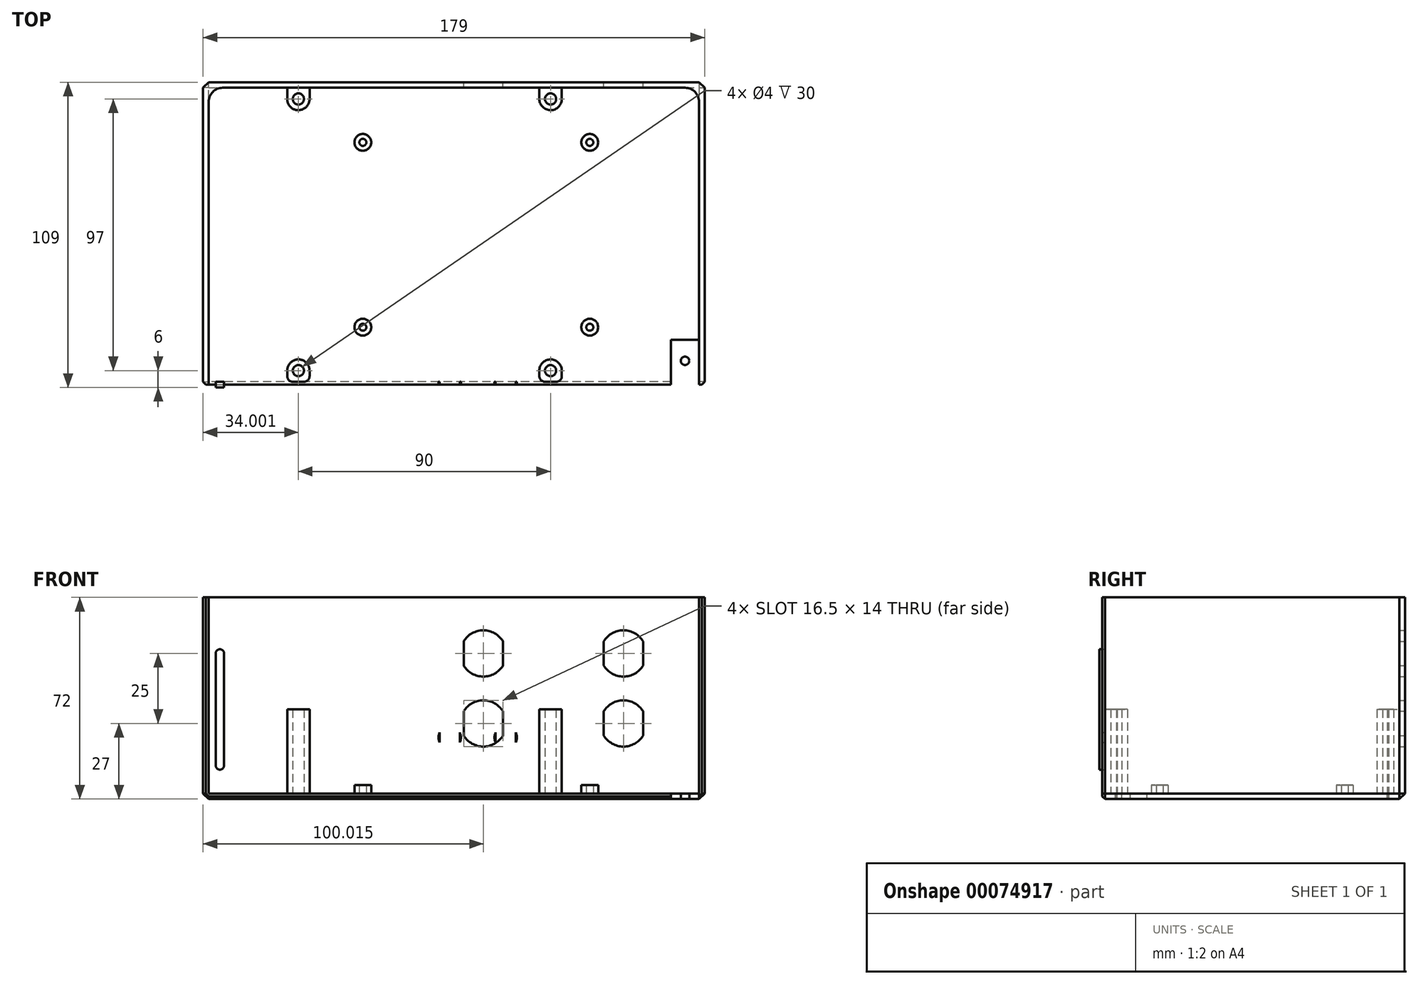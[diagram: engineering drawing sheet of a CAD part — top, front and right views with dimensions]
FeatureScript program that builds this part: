
annotation { "Feature Type Name" : "Feature", "Feature Type Description" : "" }
export const myFeature = defineFeature(function(context is Context, id is Id, definition is map)
    precondition{}
    {
        {
            var Q0;
            Q0=qCreatedBy(makeId("Top.planeOp"),FACE);
            var sketch = newSketch(context, id + "F0", { "sketchPlane" : qUnion([Q0])});
            skLineSegment(sketch, "E0.bottom", {"start": v(-80.27, 52.5) * mm, "end": v(94.73, 52.5) * mm});
            skLineSegment(sketch, "E0.top", {"start": v(-80.27, -52.5) * mm, "end": v(94.73, -52.5) * mm});
            skLineSegment(sketch, "E0.left", {"start": v(-80.27, 52.5) * mm, "end": v(-80.27, -52.5) * mm});
            skLineSegment(sketch, "E0.right", {"start": v(94.73, 52.5) * mm, "end": v(94.73, -52.5) * mm});
            skCircle(sketch, "E1", {"center": v(-25.27, 33) * mm, "radius": 1.25 * mm});
            skCircle(sketch, "E2.0.1.0", {"center": v(-25.27, -33) * mm, "radius": 1.25 * mm});
            skCircle(sketch, "E2.1.0.0", {"center": v(55.73, 33) * mm, "radius": 1.25 * mm});
            skCircle(sketch, "E2.1.1.0", {"center": v(55.73, -33) * mm, "radius": 1.25 * mm});
            skLineSegment(sketch, "E2.direction1", {"start": v(-25.27, 33) * mm, "end": v(55.73, 33) * mm, "construction": true});
            skLineSegment(sketch, "E2.direction2", {"start": v(-25.27, 33) * mm, "end": v(-25.27, -33) * mm, "construction": true});
            skLineSegment(sketch, "E3.bottom", {"start": v(-82.27, 54.5) * mm, "end": v(96.73, 54.5) * mm});
            skLineSegment(sketch, "E3.top", {"start": v(-82.27, -54.5) * mm, "end": v(96.73, -54.5) * mm});
            skLineSegment(sketch, "E3.left", {"start": v(-82.27, 54.5) * mm, "end": v(-82.27, -54.5) * mm});
            skLineSegment(sketch, "E3.right", {"start": v(96.73, 54.5) * mm, "end": v(96.73, -54.5) * mm});
            skCircle(sketch, "E4", {"center": v(-25.27, 33) * mm, "radius": 3 * mm});
            skCircle(sketch, "E5.0.1.0", {"center": v(-25.27, -33) * mm, "radius": 3 * mm});
            skCircle(sketch, "E5.1.0.0", {"center": v(55.73, 33) * mm, "radius": 3 * mm});
            skCircle(sketch, "E5.1.1.0", {"center": v(55.73, -33) * mm, "radius": 3 * mm});
            skLineSegment(sketch, "E6.bottom", {"start": v(-48.27, 42.5) * mm, "end": v(75.73, 42.5) * mm});
            skLineSegment(sketch, "E6.top", {"start": v(-48.27, -42.5) * mm, "end": v(75.73, -42.5) * mm});
            skLineSegment(sketch, "E6.left", {"start": v(-48.27, 42.5) * mm, "end": v(-48.27, -42.5) * mm});
            skLineSegment(sketch, "E6.right", {"start": v(75.73, 42.5) * mm, "end": v(75.73, -42.5) * mm});
            skCircle(sketch, "E7", {"center": v(-48.27, -48.5) * mm, "radius": 2 * mm});
            skCircle(sketch, "E8", {"center": v(-48.27, -48.5) * mm, "radius": 4 * mm});
            skCircle(sketch, "E9.0.1.0", {"center": v(-48.27, 48.5) * mm, "radius": 4 * mm});
            skCircle(sketch, "E9.0.1.1", {"center": v(-48.27, 48.5) * mm, "radius": 2 * mm});
            skCircle(sketch, "E9.1.0.0", {"center": v(41.73, -48.5) * mm, "radius": 4 * mm});
            skCircle(sketch, "E9.1.0.1", {"center": v(41.73, -48.5) * mm, "radius": 2 * mm});
            skCircle(sketch, "E9.1.1.0", {"center": v(41.73, 48.5) * mm, "radius": 4 * mm});
            skCircle(sketch, "E9.1.1.1", {"center": v(41.73, 48.5) * mm, "radius": 2 * mm});
            skLineSegment(sketch, "E9.direction1", {"start": v(-48.27, -48.5) * mm, "end": v(41.73, -48.5) * mm, "construction": true});
            skLineSegment(sketch, "E9.direction2", {"start": v(-48.27, -48.5) * mm, "end": v(-48.27, 48.5) * mm, "construction": true});
            skLineSegment(sketch, "E10", {"start": v(-52.27, -48.55) * mm, "end": v(-52.22, -52.5) * mm});
            skLineSegment(sketch, "E11", {"start": v(-44.27, -48.5) * mm, "end": v(-44.27, -52.5) * mm});
            skLineSegment(sketch, "E12", {"start": v(-52.26, 48.76) * mm, "end": v(-52.26, 52.5) * mm});
            skLineSegment(sketch, "E13", {"start": v(-44.27, 48.54) * mm, "end": v(-44.27, 52.5) * mm});
            skLineSegment(sketch, "E14", {"start": v(37.74, 48.16) * mm, "end": v(37.74, 52.5) * mm});
            skLineSegment(sketch, "E15", {"start": v(45.73, 48.44) * mm, "end": v(45.73, 52.5) * mm});
            skLineSegment(sketch, "E16.MirrorCS", {"start": v(37.74, -48.16) * mm, "end": v(37.74, -52.5) * mm});
            skLineSegment(sketch, "E17.MirrorCS", {"start": v(45.73, -48.44) * mm, "end": v(45.73, -52.5) * mm});
            skLineSegment(sketch, "E18.bottom", {"start": v(94.73, 27.5) * mm, "end": v(84.73, 27.5) * mm});
            skLineSegment(sketch, "E18.top", {"start": v(94.73, 12.5) * mm, "end": v(84.73, 12.5) * mm});
            skLineSegment(sketch, "E18.left", {"start": v(94.73, 27.5) * mm, "end": v(94.73, 12.5) * mm});
            skLineSegment(sketch, "E18.right", {"start": v(84.73, 27.5) * mm, "end": v(84.73, 12.5) * mm});
            skCircle(sketch, "E19", {"center": v(89.73, 20) * mm, "radius": 1.5 * mm});
            skPoint(sketch, "E19.centerSnap0", {"position": v(89.73, 12.5) * mm});
            skPoint(sketch, "E19.centerSnap1", {"position": v(94.73, 20) * mm});
            skLineSegment(sketch, "E20.bottom", {"start": v(94.73, -52.5) * mm, "end": v(84.73, -52.5) * mm});
            skLineSegment(sketch, "E20.top", {"start": v(94.73, -37.5) * mm, "end": v(84.73, -37.5) * mm});
            skLineSegment(sketch, "E20.left", {"start": v(94.73, -52.5) * mm, "end": v(94.73, -37.5) * mm});
            skLineSegment(sketch, "E20.right", {"start": v(84.73, -52.5) * mm, "end": v(84.73, -37.5) * mm});
            skCircle(sketch, "E21", {"center": v(89.73, -45) * mm, "radius": 1.5 * mm});
            skPoint(sketch, "E21.centerSnap0", {"position": v(94.73, -45) * mm});
            skPoint(sketch, "E21.centerSnap1", {"position": v(89.73, -52.5) * mm});
            skSolve(sketch);
        }
        {
            var Q0;
            Q0 = qSketchRegion(id + "F0", true);
            var Q1;
            Q1=makeQuery(id+"F0.imprint","IMPRINT",FACE,{"disambiguationData":[TD([[makeQuery(id+"F0.imprint","IMPRINT",EDGE,{"derivedFrom":sQuery(id+"F0.wireOp",EDGE,"E0.bottom")}),-1.0]])]});
            var Q2;
            Q2=makeQuery(id+"F0.imprint","IMPRINT",FACE,{"disambiguationData":[TD([[makeQuery(id+"F0.imprint","IMPRINT",EDGE,{"derivedFrom":sQuery(id+"F0.wireOp",EDGE,"E2.1.1.0")}),-1.0]])]});
            var Q3;
            Q3=makeQuery(id+"F0.imprint","IMPRINT",FACE,{"disambiguationData":[TD([[makeQuery(id+"F0.imprint","IMPRINT",EDGE,{"derivedFrom":sQuery(id+"F0.wireOp",EDGE,"E2.1.1.0")}),1.0]])]});
            var Q4;
            Q4=makeQuery(id+"F0.imprint","IMPRINT",FACE,{"disambiguationData":[TD([[makeQuery(id+"F0.imprint","IMPRINT",EDGE,{"derivedFrom":sQuery(id+"F0.wireOp",EDGE,"E2.0.1.0")}),-1.0]])]});
            var Q5;
            Q5=makeQuery(id+"F0.imprint","IMPRINT",FACE,{"disambiguationData":[TD([[makeQuery(id+"F0.imprint","IMPRINT",EDGE,{"derivedFrom":sQuery(id+"F0.wireOp",EDGE,"E2.0.1.0")}),1.0]])]});
            var Q6;
            Q6=makeQuery(id+"F0.imprint","IMPRINT",FACE,{"disambiguationData":[TD([[makeQuery(id+"F0.imprint","IMPRINT",EDGE,{"derivedFrom":sQuery(id+"F0.wireOp",EDGE,"E1")}),-1.0]])]});
            var Q7;
            Q7=makeQuery(id+"F0.imprint","IMPRINT",FACE,{"disambiguationData":[TD([[makeQuery(id+"F0.imprint","IMPRINT",EDGE,{"derivedFrom":sQuery(id+"F0.wireOp",EDGE,"E1")}),1.0]])]});
            var Q8;
            Q8=makeQuery(id+"F0.imprint","IMPRINT",FACE,{"disambiguationData":[TD([[makeQuery(id+"F0.imprint","IMPRINT",EDGE,{"derivedFrom":sQuery(id+"F0.wireOp",EDGE,"E2.1.0.0")}),-1.0]])]});
            var Q9;
            Q9=makeQuery(id+"F0.imprint","IMPRINT",FACE,{"disambiguationData":[TD([[makeQuery(id+"F0.imprint","IMPRINT",EDGE,{"derivedFrom":sQuery(id+"F0.wireOp",EDGE,"E2.1.0.0")}),1.0]])]});
            var Q10;
            Q10=makeQuery(id+"F0.imprint","IMPRINT",FACE,{"disambiguationData":[TD([[makeQuery(id+"F0.imprint","IMPRINT",EDGE,{"derivedFrom":sQuery(id+"F0.wireOp",EDGE,"E4")}),-1.0]])]});
            var Q11;
            Q11=makeQuery(id+"F0.imprint","IMPRINT",FACE,{"disambiguationData":[TD([[makeQuery(id+"F0.imprint","IMPRINT",EDGE,{"derivedFrom":sQuery(id+"F0.wireOp",EDGE,"E9.1.0.1")}),-1.0]])]});
            var Q12;
            Q12=makeQuery(id+"F0.imprint","IMPRINT",FACE,{"disambiguationData":[TD([[makeQuery(id+"F0.imprint","IMPRINT",EDGE,{"derivedFrom":sQuery(id+"F0.wireOp",EDGE,"E9.1.0.1")}),1.0]])]});
            var Q13;
            {var subQ0=sQuery(id+"F0.wireOp",EDGE,"E16.MirrorCS");var subQ1=sQuery(id+"F0.wireOp",EDGE,"E0.top");var subQ2=makeQuery(id+"F0.imprint","INTERSECT",VERTEX,{"derivedFrom":[subQ1,subQ0]});Q13=makeQuery(id+"F0.imprint","IMPRINT",FACE,{"disambiguationData":[TD([[makeQuery(id+"F0.imprint","IMPRINT",EDGE,{"disambiguationData":[TD([[subQ2,-1.0]])],"derivedFrom":subQ1}),1.0]])]});}
            var Q14;
            Q14=makeQuery(id+"F0.imprint","IMPRINT",FACE,{"disambiguationData":[TD([[makeQuery(id+"F0.imprint","IMPRINT",EDGE,{"derivedFrom":sQuery(id+"F0.wireOp",EDGE,"E7")}),-1.0]])]});
            var Q15;
            Q15=makeQuery(id+"F0.imprint","IMPRINT",FACE,{"disambiguationData":[TD([[makeQuery(id+"F0.imprint","IMPRINT",EDGE,{"derivedFrom":sQuery(id+"F0.wireOp",EDGE,"E7")}),1.0]])]});
            var Q16;
            {var subQ0=sQuery(id+"F0.wireOp",EDGE,"E10");Q16=makeQuery(id+"F0.imprint","IMPRINT",FACE,{"disambiguationData":[TD([[makeQuery(id+"F0.imprint","IMPRINT",EDGE,{"derivedFrom":subQ0}),1.0]])]});}
            var Q17;
            {var subQ0=sQuery(id+"F0.wireOp",EDGE,"E11");Q17=makeQuery(id+"F0.imprint","IMPRINT",FACE,{"disambiguationData":[TD([[makeQuery(id+"F0.imprint","IMPRINT",EDGE,{"derivedFrom":subQ0}),-1.0]])]});}
            var Q18;
            Q18=makeQuery(id+"F0.imprint","IMPRINT",FACE,{"disambiguationData":[TD([[makeQuery(id+"F0.imprint","IMPRINT",EDGE,{"derivedFrom":sQuery(id+"F0.wireOp",EDGE,"E9.0.1.1")}),-1.0]])]});
            var Q19;
            Q19=makeQuery(id+"F0.imprint","IMPRINT",FACE,{"disambiguationData":[TD([[makeQuery(id+"F0.imprint","IMPRINT",EDGE,{"derivedFrom":sQuery(id+"F0.wireOp",EDGE,"E9.0.1.1")}),1.0]])]});
            var Q20;
            {var subQ0=sQuery(id+"F0.wireOp",EDGE,"E13");Q20=makeQuery(id+"F0.imprint","IMPRINT",FACE,{"disambiguationData":[TD([[makeQuery(id+"F0.imprint","IMPRINT",EDGE,{"derivedFrom":subQ0}),1.0]])]});}
            var Q21;
            {var subQ0=sQuery(id+"F0.wireOp",EDGE,"E12");Q21=makeQuery(id+"F0.imprint","IMPRINT",FACE,{"disambiguationData":[TD([[makeQuery(id+"F0.imprint","IMPRINT",EDGE,{"derivedFrom":subQ0}),-1.0]])]});}
            var Q22;
            {var subQ0=sQuery(id+"F0.wireOp",EDGE,"E17.MirrorCS");var subQ1=sQuery(id+"F0.wireOp",EDGE,"E0.top");var subQ2=makeQuery(id+"F0.imprint","INTERSECT",VERTEX,{"derivedFrom":[subQ1,subQ0]});Q22=makeQuery(id+"F0.imprint","IMPRINT",FACE,{"disambiguationData":[TD([[makeQuery(id+"F0.imprint","IMPRINT",EDGE,{"disambiguationData":[TD([[subQ2,1.0]])],"derivedFrom":subQ1}),1.0]])]});}
            var Q23;
            {var subQ0=sQuery(id+"F0.wireOp",EDGE,"E14");var subQ1=sQuery(id+"F0.wireOp",EDGE,"E0.bottom");var subQ2=makeQuery(id+"F0.imprint","INTERSECT",VERTEX,{"derivedFrom":[subQ1,subQ0]});Q23=makeQuery(id+"F0.imprint","IMPRINT",FACE,{"disambiguationData":[TD([[makeQuery(id+"F0.imprint","IMPRINT",EDGE,{"disambiguationData":[TD([[subQ2,-1.0]])],"derivedFrom":subQ1}),-1.0]])]});}
            var Q24;
            {var subQ0=sQuery(id+"F0.wireOp",EDGE,"E15");var subQ1=sQuery(id+"F0.wireOp",EDGE,"E0.bottom");var subQ2=makeQuery(id+"F0.imprint","INTERSECT",VERTEX,{"derivedFrom":[subQ1,subQ0]});Q24=makeQuery(id+"F0.imprint","IMPRINT",FACE,{"disambiguationData":[TD([[makeQuery(id+"F0.imprint","IMPRINT",EDGE,{"disambiguationData":[TD([[subQ2,1.0]])],"derivedFrom":subQ1}),-1.0]])]});}
            var Q25;
            Q25=makeQuery(id+"F0.imprint","IMPRINT",FACE,{"disambiguationData":[TD([[makeQuery(id+"F0.imprint","IMPRINT",EDGE,{"derivedFrom":sQuery(id+"F0.wireOp",EDGE,"E9.1.1.1")}),-1.0]])]});
            var Q26;
            Q26=makeQuery(id+"F0.imprint","IMPRINT",FACE,{"disambiguationData":[TD([[makeQuery(id+"F0.imprint","IMPRINT",EDGE,{"derivedFrom":sQuery(id+"F0.wireOp",EDGE,"E9.1.1.1")}),1.0]])]});
            var Q27;
            Q27=makeQuery(id+"F0.imprint","IMPRINT",FACE,{"disambiguationData":[TD([[makeQuery(id+"F0.imprint","IMPRINT",EDGE,{"derivedFrom":sQuery(id+"F0.wireOp",EDGE,"E18.bottom")}),1.0]])]});
            var Q28;
            Q28=makeQuery(id+"F0.imprint","IMPRINT",FACE,{"disambiguationData":[TD([[makeQuery(id+"F0.imprint","IMPRINT",EDGE,{"derivedFrom":sQuery(id+"F0.wireOp",EDGE,"E20.bottom")}),-1.0]])]});
            var Q29;
            Q29=makeQuery(id+"F0.imprint","IMPRINT",FACE,{"disambiguationData":[TD([[makeQuery(id+"F0.imprint","IMPRINT",EDGE,{"derivedFrom":sQuery(id+"F0.wireOp",EDGE,"E19")}),1.0]])]});
            var Q30;
            Q30=makeQuery(id+"F0.imprint","IMPRINT",FACE,{"disambiguationData":[TD([[makeQuery(id+"F0.imprint","IMPRINT",EDGE,{"derivedFrom":sQuery(id+"F0.wireOp",EDGE,"E21")}),1.0]])]});
            extrude(context, id + "F1", {"entities" : qUnion([Q0, Q1, Q2, Q3, Q4, Q5, Q6, Q7, Q8, Q9, Q10, Q11, Q12, Q13, Q14, Q15, Q16, Q17, Q18, Q19, Q20, Q21, Q22, Q23, Q24, Q25, Q26, Q27, Q28, Q29, Q30]), "oppositeDirection" : true, "depth" : 2 * mm});
        }
        {
            var Q0;
            Q0=makeQuery(id+"F0.imprint","IMPRINT",FACE,{"disambiguationData":[TD([[makeQuery(id+"F0.imprint","IMPRINT",EDGE,{"derivedFrom":sQuery(id+"F0.wireOp",EDGE,"E1")}),-1.0]])]});
            var Q1;
            Q1=makeQuery(id+"F0.imprint","IMPRINT",FACE,{"disambiguationData":[TD([[makeQuery(id+"F0.imprint","IMPRINT",EDGE,{"derivedFrom":sQuery(id+"F0.wireOp",EDGE,"E2.0.1.0")}),-1.0]])]});
            var Q2;
            Q2=makeQuery(id+"F0.imprint","IMPRINT",FACE,{"disambiguationData":[TD([[makeQuery(id+"F0.imprint","IMPRINT",EDGE,{"derivedFrom":sQuery(id+"F0.wireOp",EDGE,"E2.1.0.0")}),-1.0]])]});
            var Q3;
            Q3=makeQuery(id+"F0.imprint","IMPRINT",FACE,{"disambiguationData":[TD([[makeQuery(id+"F0.imprint","IMPRINT",EDGE,{"derivedFrom":sQuery(id+"F0.wireOp",EDGE,"E2.1.1.0")}),-1.0]])]});
            extrude(context, id + "F2", {"entities" : qUnion([Q0, Q1, Q2, Q3]), "operationType" : NewBodyOperationType.ADD, "depth" : 3 * mm});
        }
        {
            var Q0;
            Q0=makeQuery(id+"F0.imprint","IMPRINT",FACE,{"disambiguationData":[TD([[makeQuery(id+"F0.imprint","IMPRINT",EDGE,{"derivedFrom":sQuery(id+"F0.wireOp",EDGE,"E0.bottom")}),1.0]])]});
            extrude(context, id + "F3", {"entities" : qUnion([Q0]), "operationType" : NewBodyOperationType.ADD, "depth" : 70 * mm});
        }
        {
            var Q0;
            Q0=makeQuery(id+"F3.opExtrude","SWEPT_FACE",FACE,{"disambiguationData":[OSD([sQuery(id+"F0.wireOp",EDGE,"E0.top"),sQuery(id+"F0.wireOp",EDGE,"E20.bottom")])]});
            var sketch = newSketch(context, id + "F4", { "sketchPlane" : qUnion([Q0])});
            skCircle(sketch, "E22", {"center": v(-64.73, 20) * mm, "radius": 5.5 * mm});
            skCircle(sketch, "E23", {"center": v(34.27, 20) * mm, "radius": 3.25 * mm});
            skCircle(sketch, "E24.1.0.0", {"center": v(14.27, 20) * mm, "radius": 3.25 * mm});
            skLineSegment(sketch, "E24.direction1", {"start": v(34.27, 20) * mm, "end": v(14.27, 20) * mm, "construction": true});
            skLineSegment(sketch, "E25", {"start": v(76.27, 50) * mm, "end": v(76.27, 10) * mm});
            skArc(sketch, "E26.0.startCap", {"start": v(74.77, 50) * mm, "mid": v(76.27, 51.5) * mm, "end": v(77.77, 50) * mm});
            skArc(sketch, "E26.0.endCap", {"start": v(77.77, 10) * mm, "mid": v(76.27, 8.5) * mm, "end": v(74.77, 10) * mm});
            skLineSegment(sketch, "E26.0.left", {"start": v(77.77, 50) * mm, "end": v(77.77, 10) * mm});
            skLineSegment(sketch, "E26.0.right", {"start": v(74.77, 50) * mm, "end": v(74.77, 10) * mm});
            skCircle(sketch, "E27", {"center": v(-5.73, 20) * mm, "radius": 4 * mm});
            skCircle(sketch, "E28.1.0.2", {"center": v(-25.73, 20) * mm, "radius": 4 * mm});
            skLineSegment(sketch, "E28.direction1", {"start": v(-9.62, 20.95) * mm, "end": v(-29.62, 20.95) * mm, "construction": true});
            skLineSegment(sketch, "E29", {"start": v(-29.33, 23.3) * mm, "end": v(-29.33, 15.56) * mm, "construction": true});
            skLineSegment(sketch, "E30", {"start": v(-29.33, 15.56) * mm, "end": v(-22.13, 15.56) * mm, "construction": true});
            skLineSegment(sketch, "E31", {"start": v(-22.13, 15.56) * mm, "end": v(-22.13, 24.42) * mm, "construction": true});
            skLineSegment(sketch, "E32", {"start": v(-22.13, 21.74) * mm, "end": v(-22.13, 18.26) * mm});
            skLineSegment(sketch, "E33", {"start": v(-29.33, 21.74) * mm, "end": v(-29.33, 18.26) * mm});
            skLineSegment(sketch, "E34.1.0.0", {"start": v(-9.33, 21.74) * mm, "end": v(-9.33, 18.26) * mm});
            skLineSegment(sketch, "E34.1.0.1", {"start": v(-2.13, 21.74) * mm, "end": v(-2.13, 18.26) * mm});
            skLineSegment(sketch, "E34.direction1", {"start": v(-29.33, 18.26) * mm, "end": v(-9.33, 18.26) * mm, "construction": true});
            skSolve(sketch);
        }
        {
            var Q0;
            Q0=makeQuery(id+"F4.imprint","IMPRINT",FACE,{"disambiguationData":[TD([[makeQuery(id+"F4.imprint","IMPRINT",EDGE,{"derivedFrom":sQuery(id+"F4.wireOp",EDGE,"E22")}),1.0]])]});
            var Q1;
            {var subQ0=sQuery(id+"F4.wireOp",EDGE,"E32");Q1=makeQuery(id+"F4.imprint","IMPRINT",FACE,{"disambiguationData":[TD([[makeQuery(id+"F4.imprint","IMPRINT",EDGE,{"derivedFrom":subQ0}),-1.0]])]});}
            var Q2;
            {var subQ0=sQuery(id+"F4.wireOp",EDGE,"E34.1.0.0");Q2=makeQuery(id+"F4.imprint","IMPRINT",FACE,{"disambiguationData":[TD([[makeQuery(id+"F4.imprint","IMPRINT",EDGE,{"derivedFrom":subQ0}),1.0]])]});}
            var Q3;
            Q3=makeQuery(id+"F4.imprint","IMPRINT",FACE,{"disambiguationData":[TD([[makeQuery(id+"F4.imprint","IMPRINT",EDGE,{"derivedFrom":sQuery(id+"F4.wireOp",EDGE,"E24.1.0.0")}),1.0]])]});
            var Q4;
            Q4=makeQuery(id+"F4.imprint","IMPRINT",FACE,{"disambiguationData":[TD([[makeQuery(id+"F4.imprint","IMPRINT",EDGE,{"derivedFrom":sQuery(id+"F4.wireOp",EDGE,"E23")}),1.0]])]});
            var Q5;
            Q5=makeQuery(id+"F4.imprint","IMPRINT",FACE,{"disambiguationData":[TD([[makeQuery(id+"F4.imprint","IMPRINT",EDGE,{"derivedFrom":sQuery(id+"F4.wireOp",EDGE,"E26.0.startCap")}),-1.0]])]});
            extrude(context, id + "F5", {"entities" : qUnion([Q0, Q1, Q2, Q3, Q4, Q5]), "operationType" : NewBodyOperationType.REMOVE, "endBound" : BoundingType.UP_TO_NEXT, "oppositeDirection" : true, "depth" : 25 * mm});
        }
        {
            var Q0;
            Q0=makeQuery(id+"F0.imprint","IMPRINT",FACE,{"disambiguationData":[TD([[makeQuery(id+"F0.imprint","IMPRINT",EDGE,{"derivedFrom":sQuery(id+"F0.wireOp",EDGE,"E9.0.1.1")}),-1.0]])]});
            var Q1;
            {var subQ0=sQuery(id+"F0.wireOp",EDGE,"E12");Q1=makeQuery(id+"F0.imprint","IMPRINT",FACE,{"disambiguationData":[TD([[makeQuery(id+"F0.imprint","IMPRINT",EDGE,{"derivedFrom":subQ0}),-1.0]])]});}
            var Q2;
            {var subQ0=sQuery(id+"F0.wireOp",EDGE,"E13");Q2=makeQuery(id+"F0.imprint","IMPRINT",FACE,{"disambiguationData":[TD([[makeQuery(id+"F0.imprint","IMPRINT",EDGE,{"derivedFrom":subQ0}),1.0]])]});}
            var Q3;
            {var subQ0=sQuery(id+"F0.wireOp",EDGE,"E14");var subQ1=sQuery(id+"F0.wireOp",EDGE,"E0.bottom");var subQ2=makeQuery(id+"F0.imprint","INTERSECT",VERTEX,{"derivedFrom":[subQ1,subQ0]});Q3=makeQuery(id+"F0.imprint","IMPRINT",FACE,{"disambiguationData":[TD([[makeQuery(id+"F0.imprint","IMPRINT",EDGE,{"disambiguationData":[TD([[subQ2,-1.0]])],"derivedFrom":subQ1}),-1.0]])]});}
            var Q4;
            {var subQ0=sQuery(id+"F0.wireOp",EDGE,"E15");var subQ1=sQuery(id+"F0.wireOp",EDGE,"E0.bottom");var subQ2=makeQuery(id+"F0.imprint","INTERSECT",VERTEX,{"derivedFrom":[subQ1,subQ0]});Q4=makeQuery(id+"F0.imprint","IMPRINT",FACE,{"disambiguationData":[TD([[makeQuery(id+"F0.imprint","IMPRINT",EDGE,{"disambiguationData":[TD([[subQ2,1.0]])],"derivedFrom":subQ1}),-1.0]])]});}
            var Q5;
            Q5=makeQuery(id+"F0.imprint","IMPRINT",FACE,{"disambiguationData":[TD([[makeQuery(id+"F0.imprint","IMPRINT",EDGE,{"derivedFrom":sQuery(id+"F0.wireOp",EDGE,"E9.1.1.1")}),-1.0]])]});
            var Q6;
            Q6=makeQuery(id+"F0.imprint","IMPRINT",FACE,{"disambiguationData":[TD([[makeQuery(id+"F0.imprint","IMPRINT",EDGE,{"derivedFrom":sQuery(id+"F0.wireOp",EDGE,"E7")}),-1.0]])]});
            var Q7;
            {var subQ0=sQuery(id+"F0.wireOp",EDGE,"E10");Q7=makeQuery(id+"F0.imprint","IMPRINT",FACE,{"disambiguationData":[TD([[makeQuery(id+"F0.imprint","IMPRINT",EDGE,{"derivedFrom":subQ0}),1.0]])]});}
            var Q8;
            {var subQ0=sQuery(id+"F0.wireOp",EDGE,"E11");Q8=makeQuery(id+"F0.imprint","IMPRINT",FACE,{"disambiguationData":[TD([[makeQuery(id+"F0.imprint","IMPRINT",EDGE,{"derivedFrom":subQ0}),-1.0]])]});}
            var Q9;
            {var subQ0=sQuery(id+"F0.wireOp",EDGE,"E16.MirrorCS");var subQ1=sQuery(id+"F0.wireOp",EDGE,"E0.top");var subQ2=makeQuery(id+"F0.imprint","INTERSECT",VERTEX,{"derivedFrom":[subQ1,subQ0]});Q9=makeQuery(id+"F0.imprint","IMPRINT",FACE,{"disambiguationData":[TD([[makeQuery(id+"F0.imprint","IMPRINT",EDGE,{"disambiguationData":[TD([[subQ2,-1.0]])],"derivedFrom":subQ1}),1.0]])]});}
            var Q10;
            Q10=makeQuery(id+"F0.imprint","IMPRINT",FACE,{"disambiguationData":[TD([[makeQuery(id+"F0.imprint","IMPRINT",EDGE,{"derivedFrom":sQuery(id+"F0.wireOp",EDGE,"E9.1.0.1")}),-1.0]])]});
            var Q11;
            {var subQ0=sQuery(id+"F0.wireOp",EDGE,"E17.MirrorCS");var subQ1=sQuery(id+"F0.wireOp",EDGE,"E0.top");var subQ2=makeQuery(id+"F0.imprint","INTERSECT",VERTEX,{"derivedFrom":[subQ1,subQ0]});Q11=makeQuery(id+"F0.imprint","IMPRINT",FACE,{"disambiguationData":[TD([[makeQuery(id+"F0.imprint","IMPRINT",EDGE,{"disambiguationData":[TD([[subQ2,1.0]])],"derivedFrom":subQ1}),1.0]])]});}
            extrude(context, id + "F6", {"entities" : qUnion([Q0, Q1, Q2, Q3, Q4, Q5, Q6, Q7, Q8, Q9, Q10, Q11]), "operationType" : NewBodyOperationType.ADD, "depth" : 30 * mm});
        }
        {
            var Q0;
            Q0=makeQuery(id+"F6.opExtrude","SWEPT_EDGE",EDGE,{"disambiguationData":[OSD([sQuery(id+"F0.wireOp",EDGE,"E0.top"),sQuery(id+"F0.wireOp",EDGE,"E10")])]});
            var Q1;
            Q1=makeQuery(id+"F6.opExtrude","SWEPT_EDGE",EDGE,{"disambiguationData":[OSD([sQuery(id+"F0.wireOp",EDGE,"E0.top"),sQuery(id+"F0.wireOp",EDGE,"E11")])]});
            var Q2;
            Q2=makeQuery(id+"F6.opExtrude","SWEPT_EDGE",EDGE,{"disambiguationData":[OSD([sQuery(id+"F0.wireOp",EDGE,"E0.top"),sQuery(id+"F0.wireOp",EDGE,"E16.MirrorCS")])]});
            var Q3;
            Q3=makeQuery(id+"F6.opExtrude","SWEPT_EDGE",EDGE,{"disambiguationData":[OSD([sQuery(id+"F0.wireOp",EDGE,"E0.top"),sQuery(id+"F0.wireOp",EDGE,"E17.MirrorCS")])]});
            var Q4;
            Q4=makeQuery(id+"F6.opExtrude","SWEPT_EDGE",EDGE,{"disambiguationData":[OSD([sQuery(id+"F0.wireOp",EDGE,"E0.bottom"),sQuery(id+"F0.wireOp",EDGE,"E15")])]});
            var Q5;
            Q5=makeQuery(id+"F6.opExtrude","SWEPT_EDGE",EDGE,{"disambiguationData":[OSD([sQuery(id+"F0.wireOp",EDGE,"E0.bottom"),sQuery(id+"F0.wireOp",EDGE,"E14")])]});
            var Q6;
            Q6=makeQuery(id+"F6.opExtrude","SWEPT_EDGE",EDGE,{"disambiguationData":[OSD([sQuery(id+"F0.wireOp",EDGE,"E0.bottom"),sQuery(id+"F0.wireOp",EDGE,"E13")])]});
            var Q7;
            Q7=makeQuery(id+"F6.opExtrude","SWEPT_EDGE",EDGE,{"disambiguationData":[OSD([sQuery(id+"F0.wireOp",EDGE,"E0.bottom"),sQuery(id+"F0.wireOp",EDGE,"E12")])]});
            fillet(context, id + "F7", {"entities" : qUnion([Q0, Q1, Q2, Q3, Q4, Q5, Q6, Q7]), "radius" : 2 * mm, "tangentPropagation" : true, "allowEdgeOverflow" : false});
        }
        {
            var Q0;
            Q0=makeQuery(id+"F3.opExtrude","SWEPT_EDGE",EDGE,{"disambiguationData":[OSD([sQuery(id+"F0.wireOp",EDGE,"E0.top"),sQuery(id+"F0.wireOp",EDGE,"E0.right")])]});
            var Q1;
            Q1=makeQuery(id+"F3.opExtrude","SWEPT_EDGE",EDGE,{"disambiguationData":[OSD([sQuery(id+"F0.wireOp",EDGE,"E0.top"),sQuery(id+"F0.wireOp",EDGE,"E0.left")])]});
            var Q2;
            Q2=makeQuery(id+"F3.opExtrude","SWEPT_EDGE",EDGE,{"disambiguationData":[OSD([sQuery(id+"F0.wireOp",EDGE,"E0.bottom"),sQuery(id+"F0.wireOp",EDGE,"E0.right")])]});
            var Q3;
            Q3=makeQuery(id+"F3.opExtrude","SWEPT_EDGE",EDGE,{"disambiguationData":[OSD([sQuery(id+"F0.wireOp",EDGE,"E0.bottom"),sQuery(id+"F0.wireOp",EDGE,"E0.left")])]});
            var Q4;
            Q4=makeQuery(id+"FWUeCJMCAEF3pSk_1.opExtrude","SWEPT_EDGE",EDGE,{"disambiguationData":[OSD([sQuery(id+"F0.wireOp",EDGE,"E0.top"),sQuery(id+"F0.wireOp",EDGE,"E20.bottom"),sQuery(id+"F0.wireOp",EDGE,"E20.right")])]});
            var Q5;
            Q5=makeQuery(id+"FWUeCJMCAEF3pSk_1.opExtrude","SWEPT_EDGE",EDGE,{"disambiguationData":[OSD([sQuery(id+"F0.wireOp",EDGE,"E0.right"),sQuery(id+"F0.wireOp",EDGE,"E20.top"),sQuery(id+"F0.wireOp",EDGE,"E20.left")])]});
            var Q6;
            Q6=makeQuery(id+"FWUeCJMCAEF3pSk_1.opExtrude","SWEPT_EDGE",EDGE,{"disambiguationData":[OSD([sQuery(id+"F0.wireOp",EDGE,"E0.right"),sQuery(id+"F0.wireOp",EDGE,"E18.top"),sQuery(id+"F0.wireOp",EDGE,"E18.left")])]});
            var Q7;
            Q7=makeQuery(id+"FWUeCJMCAEF3pSk_1.opExtrude","SWEPT_EDGE",EDGE,{"disambiguationData":[OSD([sQuery(id+"F0.wireOp",EDGE,"E0.right"),sQuery(id+"F0.wireOp",EDGE,"E18.bottom"),sQuery(id+"F0.wireOp",EDGE,"E18.left")])]});
            var Q8;
            Q8=makeQuery(id+"F3.opExtrude","SWEPT_EDGE",EDGE,{"disambiguationData":[OSD([sQuery(id+"F0.wireOp",EDGE,"E20.bottom"),sQuery(id+"F0.wireOp",EDGE,"E20.left")])]});
            fillet(context, id + "F8", {"entities" : qUnion([Q0, Q1, Q2, Q3, Q4, Q5, Q6, Q7, Q8]), "radius" : 5 * mm, "tangentPropagation" : true, "allowEdgeOverflow" : false});
        }
        {
            var Q0;
            {var subQ0=sQuery(id+"F0.wireOp",EDGE,"E3.left");var subQ1=sQuery(id+"F0.wireOp",EDGE,"E3.top");Q0=makeQuery(id+"F3.boolean.opBoolean","MERGE",EDGE,{"derivedFrom":[makeQuery(id+"F1.opExtrude","SWEPT_EDGE",EDGE,{"disambiguationData":[OSD([subQ1,subQ0])]}),makeQuery(id+"F3.opExtrude","SWEPT_EDGE",EDGE,{"disambiguationData":[OSD([subQ1,subQ0])]})]});}
            var Q1;
            {var subQ0=sQuery(id+"F0.wireOp",EDGE,"E3.left");var subQ1=sQuery(id+"F0.wireOp",EDGE,"E3.bottom");Q1=makeQuery(id+"F3.boolean.opBoolean","MERGE",EDGE,{"derivedFrom":[makeQuery(id+"F1.opExtrude","SWEPT_EDGE",EDGE,{"disambiguationData":[OSD([subQ1,subQ0])]}),makeQuery(id+"F3.opExtrude","SWEPT_EDGE",EDGE,{"disambiguationData":[OSD([subQ1,subQ0])]})]});}
            var Q2;
            {var subQ0=sQuery(id+"F0.wireOp",EDGE,"E3.right");var subQ1=sQuery(id+"F0.wireOp",EDGE,"E3.bottom");Q2=makeQuery(id+"F3.boolean.opBoolean","MERGE",EDGE,{"derivedFrom":[makeQuery(id+"F1.opExtrude","SWEPT_EDGE",EDGE,{"disambiguationData":[OSD([subQ1,subQ0])]}),makeQuery(id+"F3.opExtrude","SWEPT_EDGE",EDGE,{"disambiguationData":[OSD([subQ1,subQ0])]})]});}
            var Q3;
            {var subQ0=sQuery(id+"F0.wireOp",EDGE,"E3.right");var subQ1=sQuery(id+"F0.wireOp",EDGE,"E3.top");Q3=makeQuery(id+"F3.boolean.opBoolean","MERGE",EDGE,{"derivedFrom":[makeQuery(id+"F1.opExtrude","SWEPT_EDGE",EDGE,{"disambiguationData":[OSD([subQ1,subQ0])]}),makeQuery(id+"F3.opExtrude","SWEPT_EDGE",EDGE,{"disambiguationData":[OSD([subQ1,subQ0])]})]});}
            var Q4;
            Q4=makeQuery(id+"F1.opExtrude","CAP_EDGE",EDGE,{"disambiguationData":[OSD([sQuery(id+"F0.wireOp",EDGE,"E3.right")])],"isStart":false});
            var Q5;
            Q5=makeQuery(id+"F1.opExtrude","CAP_EDGE",EDGE,{"disambiguationData":[OSD([sQuery(id+"F0.wireOp",EDGE,"E3.left")])],"isStart":false});
            var Q6;
            Q6=makeQuery(id+"F1.opExtrude","CAP_EDGE",EDGE,{"disambiguationData":[OSD([sQuery(id+"F0.wireOp",EDGE,"E3.top")])],"isStart":false});
            var Q7;
            Q7=makeQuery(id+"F1.opExtrude","CAP_EDGE",EDGE,{"disambiguationData":[OSD([sQuery(id+"F0.wireOp",EDGE,"E3.bottom")])],"isStart":false});
            chamfer(context, id + "F9", {"entities" : qUnion([Q0, Q1, Q2, Q3, Q4, Q5, Q6, Q7]), "width" : 2 * mm, "tangentPropagation" : true});
        }
        {
            var Q0;
            {var subQ0=sQuery(id+"F0.wireOp",EDGE,"E3.top");Q0=makeQuery(id+"F3.boolean.opBoolean","MERGE",FACE,{"derivedFrom":[makeQuery(id+"F1.opExtrude","SWEPT_FACE",FACE,{"disambiguationData":[OSD([subQ0])]}),makeQuery(id+"F3.opExtrude","SWEPT_FACE",FACE,{"disambiguationData":[OSD([subQ0])]})]});}
            var sketch = newSketch(context, id + "F10", { "sketchPlane" : qUnion([Q0])});
            skArc(sketch, "E35", {"start": v(-37.74, 34.14) * mm, "mid": v(-34.27, 35.58) * mm, "end": v(-30.8, 34.14) * mm, "construction": true});
            skLineSegment(sketch, "E36", {"start": v(-34.27, 30.68) * mm, "end": v(-37.74, 34.14) * mm, "construction": true});
            skLineSegment(sketch, "E37", {"start": v(-34.27, 30.68) * mm, "end": v(-34.27, 42.11) * mm, "construction": true});
            skLineSegment(sketch, "E38", {"start": v(-34.27, 30.68) * mm, "end": v(-30.8, 34.14) * mm, "construction": true});
            skArc(sketch, "E39.0", {"start": v(-41.27, 37.68) * mm, "mid": v(-34.27, 40.58) * mm, "end": v(-27.26, 37.68) * mm, "construction": true});
            skLineSegment(sketch, "E40.0", {"start": v(-84.27, -8) * mm, "end": v(98.73, -8) * mm});
            skLineSegment(sketch, "E40.1", {"start": v(-84.27, 75) * mm, "end": v(-84.27, -8) * mm});
            skLineSegment(sketch, "E40.2", {"start": v(98.73, 75) * mm, "end": v(-84.27, 75) * mm});
            skLineSegment(sketch, "E40.3", {"start": v(98.73, -8) * mm, "end": v(98.73, 75) * mm});
            skArc(sketch, "E41.0", {"start": v(-44.8, 41.22) * mm, "mid": v(-34.27, 45.58) * mm, "end": v(-23.73, 41.22) * mm, "construction": true});
            skArc(sketch, "E42.0.startCap", {"start": v(-44.1, 40.5) * mm, "mid": v(-45.52, 40.5) * mm, "end": v(-45.52, 41.92) * mm});
            skArc(sketch, "E42.0.endCap", {"start": v(-23.02, 41.92) * mm, "mid": v(-23.02, 40.5) * mm, "end": v(-24.44, 40.5) * mm});
            skArc(sketch, "E42.0.left", {"start": v(-45.52, 41.92) * mm, "mid": v(-34.27, 46.58) * mm, "end": v(-23.02, 41.92) * mm});
            skArc(sketch, "E42.0.right", {"start": v(-44.1, 40.5) * mm, "mid": v(-34.27, 44.58) * mm, "end": v(-24.44, 40.5) * mm});
            skArc(sketch, "E43.0.startCap", {"start": v(-40.57, 36.97) * mm, "mid": v(-41.98, 36.97) * mm, "end": v(-41.98, 38.39) * mm});
            skArc(sketch, "E43.0.endCap", {"start": v(-26.56, 38.39) * mm, "mid": v(-26.56, 36.97) * mm, "end": v(-27.97, 36.97) * mm});
            skArc(sketch, "E43.0.left", {"start": v(-41.98, 38.39) * mm, "mid": v(-34.27, 41.58) * mm, "end": v(-26.56, 38.39) * mm});
            skArc(sketch, "E43.0.right", {"start": v(-40.57, 36.97) * mm, "mid": v(-34.27, 39.58) * mm, "end": v(-27.97, 36.97) * mm});
            skArc(sketch, "E43.1.startCap", {"start": v(-37.03, 33.44) * mm, "mid": v(-38.45, 33.44) * mm, "end": v(-38.45, 34.85) * mm});
            skArc(sketch, "E43.1.endCap", {"start": v(-30.1, 34.85) * mm, "mid": v(-30.1, 33.44) * mm, "end": v(-31.5, 33.44) * mm});
            skArc(sketch, "E43.1.left", {"start": v(-38.45, 34.85) * mm, "mid": v(-34.27, 36.58) * mm, "end": v(-30.1, 34.85) * mm});
            skArc(sketch, "E43.1.right", {"start": v(-37.03, 33.44) * mm, "mid": v(-34.27, 34.58) * mm, "end": v(-31.5, 33.44) * mm});
            skLineSegment(sketch, "E44", {"start": v(-14.27, 20) * mm, "end": v(-14.27, 54.13) * mm, "construction": true});
            skLineSegment(sketch, "E45", {"start": v(-14.27, 30.68) * mm, "end": v(-14.27, 54.13) * mm, "construction": true});
            skLineSegment(sketch, "E46", {"start": v(-14.27, 46.58) * mm, "end": v(-21, 54.13) * mm, "construction": true});
            skPoint(sketch, "E46.startSnap0", {"position": v(-34.27, 46.58) * mm});
            skLineSegment(sketch, "E47.MirrorCS", {"start": v(-14.27, 46.58) * mm, "end": v(-7.53, 54.13) * mm, "construction": true});
            skArc(sketch, "E48.0.endCap", {"start": v(-21.75, 53.47) * mm, "mid": v(-21.67, 54.88) * mm, "end": v(-20.26, 54.8) * mm});
            skLineSegment(sketch, "E48.0.left", {"start": v(-15.27, 46.2) * mm, "end": v(-21.75, 53.47) * mm});
            skArc(sketch, "E48.1.startCap", {"start": v(-13.27, 30.68) * mm, "mid": v(-14.27, 29.68) * mm, "end": v(-15.27, 30.68) * mm});
            skArc(sketch, "E48.1.endCap", {"start": v(-15.27, 54.13) * mm, "mid": v(-14.27, 55.13) * mm, "end": v(-13.27, 54.13) * mm});
            skLineSegment(sketch, "E48.1.left", {"start": v(-15.27, 30.68) * mm, "end": v(-15.27, 46.2) * mm});
            skLineSegment(sketch, "E48.1.right", {"start": v(-13.27, 30.68) * mm, "end": v(-13.27, 46.2) * mm});
            skArc(sketch, "E48.2.endCap", {"start": v(-8.28, 54.8) * mm, "mid": v(-6.86, 54.88) * mm, "end": v(-6.78, 53.47) * mm});
            skLineSegment(sketch, "E48.2.right", {"start": v(-13.27, 46.2) * mm, "end": v(-6.78, 53.47) * mm});
            skFitSpline(sketch, "E49", {"points": [v(4.97, 32.4) * mm, v(9.8, 35.55) * mm, v(10.9, 40.93) * mm, v(12.76, 47.98) * mm, v(15.73, 49.65) * mm], "startDerivative": vector(22.47, 10.26) * mm, "endDerivative": vector(16.5, 4.85) * mm});
            skLineSegment(sketch, "E50", {"start": v(6.9, 33.32) * mm, "end": v(6.9, 31.48) * mm});
            skLineSegment(sketch, "E51", {"start": v(6.9, 31.48) * mm, "end": v(15.73, 31.48) * mm});
            skLineSegment(sketch, "E52", {"start": v(15.73, 49.65) * mm, "end": v(15.73, 31.48) * mm, "construction": true});
            skFitSpline(sketch, "E53.MirrorCS", {"points": [v(26.5, 32.4) * mm, v(21.67, 35.55) * mm, v(20.55, 40.93) * mm, v(18.7, 47.98) * mm, v(15.73, 49.65) * mm], "startDerivative": vector(-22.47, 10.26) * mm, "endDerivative": vector(-16.5, 4.85) * mm});
            skLineSegment(sketch, "E54.MirrorCS", {"start": v(24.55, 33.32) * mm, "end": v(24.55, 31.48) * mm});
            skLineSegment(sketch, "E55.MirrorCS", {"start": v(24.55, 31.48) * mm, "end": v(15.73, 31.48) * mm});
            skArc(sketch, "E56", {"start": v(16.96, 31.48) * mm, "mid": v(15.73, 30.25) * mm, "end": v(14.5, 31.48) * mm});
            skPoint(sketch, "E57.orphan", {"position": v(15.73, 30.25) * mm});
            skPoint(sketch, "E58.orphan", {"position": v(70.94, 44.45) * mm});
            skPoint(sketch, "E59.1.4", {"position": v(71.6, 50.06) * mm});
            skLineSegment(sketch, "E59.2.0", {"start": v(65.73, 40.4) * mm, "end": v(55.73, 46.17) * mm});
            skLineSegment(sketch, "E59.2.1", {"start": v(59.73, 30) * mm, "end": v(74.4, 42.31) * mm});
            skLineSegment(sketch, "E59.2.2", {"start": v(64.4, 48.09) * mm, "end": v(74.4, 42.31) * mm});
            skLineSegment(sketch, "E59.2.3", {"start": v(70.4, 58.48) * mm, "end": v(55.73, 46.17) * mm});
            skPoint(sketch, "E59.2.4", {"position": v(66.41, 47.83) * mm});
            skLineSegment(sketch, "E60", {"start": v(65.73, 40.4) * mm, "end": v(59.73, 30) * mm});
            skLineSegment(sketch, "E61", {"start": v(64.4, 48.09) * mm, "end": v(70.4, 58.48) * mm});
            skText(sketch, "E62", { "text": "1", "fontName": "DroidSansMono.ttf"});
            skText(sketch, "E63", { "text": "2", "fontName": "DroidSansMono.ttf"});
            skLineSegment(sketch, "E64.trimOffspring", {"start": v(-15.27, 49.2) * mm, "end": v(-15.27, 54.13) * mm});
            skLineSegment(sketch, "E65.trimOffspring", {"start": v(-15.27, 49.2) * mm, "end": v(-20.26, 54.8) * mm});
            skLineSegment(sketch, "E66.trimOffspring", {"start": v(-13.27, 49.2) * mm, "end": v(-13.27, 54.13) * mm});
            skLineSegment(sketch, "E67.trimOffspring", {"start": v(-13.27, 49.2) * mm, "end": v(-8.28, 54.8) * mm});
            const initialGuessF10  = {"E62": [0.00217, 0.00538, 1, 0, 0.00778], "E63": [0.0221, 0.00538, 1, 0, 0.00778]};
            skSetInitialGuess(sketch, initialGuessF10);
            skSolve(sketch);
        }
        {
            var Q0;
            Q0=makeQuery(id+"F10.imprint","IMPRINT",FACE,{"disambiguationData":[TD([[makeQuery(id+"F10.imprint","IMPRINT",EDGE,{"derivedFrom":sQuery(id+"F10.wireOp",EDGE,"E42.0.startCap")}),-1.0]])]});
            var Q1;
            Q1=makeQuery(id+"F10.imprint","IMPRINT",FACE,{"disambiguationData":[TD([[makeQuery(id+"F10.imprint","IMPRINT",EDGE,{"derivedFrom":sQuery(id+"F10.wireOp",EDGE,"E43.0.startCap")}),-1.0]])]});
            var Q2;
            Q2=makeQuery(id+"F10.imprint","IMPRINT",FACE,{"disambiguationData":[TD([[makeQuery(id+"F10.imprint","IMPRINT",EDGE,{"derivedFrom":sQuery(id+"F10.wireOp",EDGE,"E43.1.startCap")}),-1.0]])]});
            var Q3;
            Q3=makeQuery(id+"F10.imprint","IMPRINT",FACE,{"disambiguationData":[TD([[makeQuery(id+"F10.imprint","IMPRINT",EDGE,{"derivedFrom":sQuery(id+"F10.wireOp",EDGE,"E49")}),-1.0]])]});
            var Q4;
            {var subQ3=sQuery(id+"F10.wireOp",EDGE,"E56");Q4=makeQuery(id+"F10.imprint","IMPRINT",FACE,{"disambiguationData":[TD([[makeQuery(id+"F10.imprint","IMPRINT",EDGE,{"derivedFrom":subQ3}),-1.0]])]});}
            var Q5;
            Q5=makeQuery(id+"F10.imprint","IMPRINT",FACE,{"disambiguationData":[TD([[makeQuery(id+"F10.imprint","IMPRINT",EDGE,{"derivedFrom":sQuery(id+"F10.wireOp",EDGE,"E62.sketch_text.stroke-0")}),-1.0]])]});
            var Q6;
            Q6=makeQuery(id+"F10.imprint","IMPRINT",FACE,{"disambiguationData":[TD([[makeQuery(id+"F10.imprint","IMPRINT",EDGE,{"derivedFrom":sQuery(id+"F10.wireOp",EDGE,"E63.sketch_text.stroke-0")}),-1.0]])]});
            var Q7;
            Q7=makeQuery(id+"F10.imprint","IMPRINT",FACE,{"disambiguationData":[TD([[makeQuery(id+"F10.imprint","IMPRINT",EDGE,{"derivedFrom":sQuery(id+"F10.wireOp",EDGE,"E59.2.0")}),-1.0]])]});
            var Q8;
            Q8=makeQuery(id+"F10.imprint","IMPRINT",FACE,{"disambiguationData":[TD([[makeQuery(id+"F10.imprint","IMPRINT",EDGE,{"derivedFrom":sQuery(id+"F10.wireOp",EDGE,"E48.0.endCap")}),-1.0]])]});
            extrude(context, id + "F11", {"entities" : qUnion([Q0, Q1, Q2, Q3, Q4, Q5, Q6, Q7, Q8]), "operationType" : NewBodyOperationType.REMOVE, "oppositeDirection" : true, "depth" : 1 * mm});
        }
        {
            var Q0;
            {var subQ0=sQuery(id+"F0.wireOp",EDGE,"E3.bottom");Q0=makeQuery(id+"F3.boolean.opBoolean","MERGE",FACE,{"derivedFrom":[makeQuery(id+"F1.opExtrude","SWEPT_FACE",FACE,{"disambiguationData":[OSD([subQ0])]}),makeQuery(id+"F3.opExtrude","SWEPT_FACE",FACE,{"disambiguationData":[OSD([subQ0])]})]});}
            var sketch = newSketch(context, id + "F12", { "sketchPlane" : qUnion([Q0])});
            skCircle(sketch, "E68", {"center": v(-67.74, 25) * mm, "radius": 8.25 * mm});
            skLineSegment(sketch, "E69", {"start": v(-74.74, 30.49) * mm, "end": v(-74.74, 3.5) * mm, "construction": true});
            skLineSegment(sketch, "E70", {"start": v(-60.74, 36.2) * mm, "end": v(-60.74, 10.6) * mm, "construction": true});
            skLineSegment(sketch, "E71", {"start": v(-60.74, 29.37) * mm, "end": v(-60.74, 20.63) * mm});
            skLineSegment(sketch, "E72", {"start": v(-74.74, 20.63) * mm, "end": v(-74.74, 29.37) * mm});
            skCircle(sketch, "E73.1.0.0", {"center": v(-17.74, 25) * mm, "radius": 8.25 * mm});
            skLineSegment(sketch, "E73.1.0.1", {"start": v(-10.74, 29.37) * mm, "end": v(-10.74, 20.63) * mm});
            skLineSegment(sketch, "E73.1.0.2", {"start": v(-24.74, 20.63) * mm, "end": v(-24.74, 29.37) * mm});
            skLineSegment(sketch, "E73.direction1", {"start": v(-67.74, 25) * mm, "end": v(-17.74, 25) * mm, "construction": true});
            skLineSegment(sketch, "E74.1.0.0", {"start": v(25.26, 20.63) * mm, "end": v(25.26, 29.37) * mm});
            skCircle(sketch, "E74.1.0.1", {"center": v(32.26, 25) * mm, "radius": 8.25 * mm});
            skLineSegment(sketch, "E74.1.0.2", {"start": v(39.26, 29.37) * mm, "end": v(39.26, 20.63) * mm});
            skLineSegment(sketch, "E74.direction1", {"start": v(-24.74, 20.63) * mm, "end": v(25.26, 20.63) * mm, "construction": true});
            skCircle(sketch, "E75.1.0.0", {"center": v(72.26, 25) * mm, "radius": 8.25 * mm});
            skLineSegment(sketch, "E75.1.0.1", {"start": v(79.26, 29.37) * mm, "end": v(79.26, 20.63) * mm});
            skLineSegment(sketch, "E75.1.0.2", {"start": v(65.26, 20.63) * mm, "end": v(65.26, 29.37) * mm});
            skLineSegment(sketch, "E75.direction1", {"start": v(32.26, 25) * mm, "end": v(72.26, 25) * mm, "construction": true});
            skCircle(sketch, "E76.0.1.0", {"center": v(-67.74, 50) * mm, "radius": 8.25 * mm});
            skLineSegment(sketch, "E76.0.1.1", {"start": v(-74.74, 45.63) * mm, "end": v(-74.74, 54.37) * mm});
            skLineSegment(sketch, "E76.0.1.2", {"start": v(-60.74, 54.37) * mm, "end": v(-60.74, 45.63) * mm});
            skLineSegment(sketch, "E76.direction1", {"start": v(-67.74, 25) * mm, "end": v(-32.74, 25) * mm, "construction": true});
            skLineSegment(sketch, "E76.direction2", {"start": v(-67.74, 25) * mm, "end": v(-67.74, 50) * mm, "construction": true});
            skCircle(sketch, "E77.0.1.0", {"center": v(-17.74, 50) * mm, "radius": 8.25 * mm});
            skLineSegment(sketch, "E77.0.1.1", {"start": v(-24.74, 45.63) * mm, "end": v(-24.74, 54.37) * mm});
            skLineSegment(sketch, "E77.0.1.2", {"start": v(-10.74, 54.37) * mm, "end": v(-10.74, 45.63) * mm});
            skLineSegment(sketch, "E77.direction1", {"start": v(-17.74, 25) * mm, "end": v(7.26, 25) * mm, "construction": true});
            skLineSegment(sketch, "E77.direction2", {"start": v(-17.74, 25) * mm, "end": v(-17.74, 50) * mm, "construction": true});
            skSolve(sketch);
        }
        {
            var Q0;
            {var subQ0=sQuery(id+"F12.wireOp",EDGE,"E76.0.1.1");Q0=makeQuery(id+"F12.imprint","IMPRINT",FACE,{"disambiguationData":[TD([[makeQuery(id+"F12.imprint","IMPRINT",EDGE,{"derivedFrom":subQ0}),-1.0]])]});}
            var Q1;
            {var subQ0=sQuery(id+"F12.wireOp",EDGE,"E71");Q1=makeQuery(id+"F12.imprint","IMPRINT",FACE,{"disambiguationData":[TD([[makeQuery(id+"F12.imprint","IMPRINT",EDGE,{"derivedFrom":subQ0}),-1.0]])]});}
            var Q2;
            {var subQ0=sQuery(id+"F12.wireOp",EDGE,"E77.0.1.1");Q2=makeQuery(id+"F12.imprint","IMPRINT",FACE,{"disambiguationData":[TD([[makeQuery(id+"F12.imprint","IMPRINT",EDGE,{"derivedFrom":subQ0}),-1.0]])]});}
            var Q3;
            {var subQ0=sQuery(id+"F12.wireOp",EDGE,"E73.1.0.1");Q3=makeQuery(id+"F12.imprint","IMPRINT",FACE,{"disambiguationData":[TD([[makeQuery(id+"F12.imprint","IMPRINT",EDGE,{"derivedFrom":subQ0}),-1.0]])]});}
            extrude(context, id + "F13", {"entities" : qUnion([Q0, Q1, Q2, Q3]), "operationType" : NewBodyOperationType.REMOVE, "endBound" : BoundingType.UP_TO_NEXT, "oppositeDirection" : true, "depth" : 25 * mm});
        }
    });
